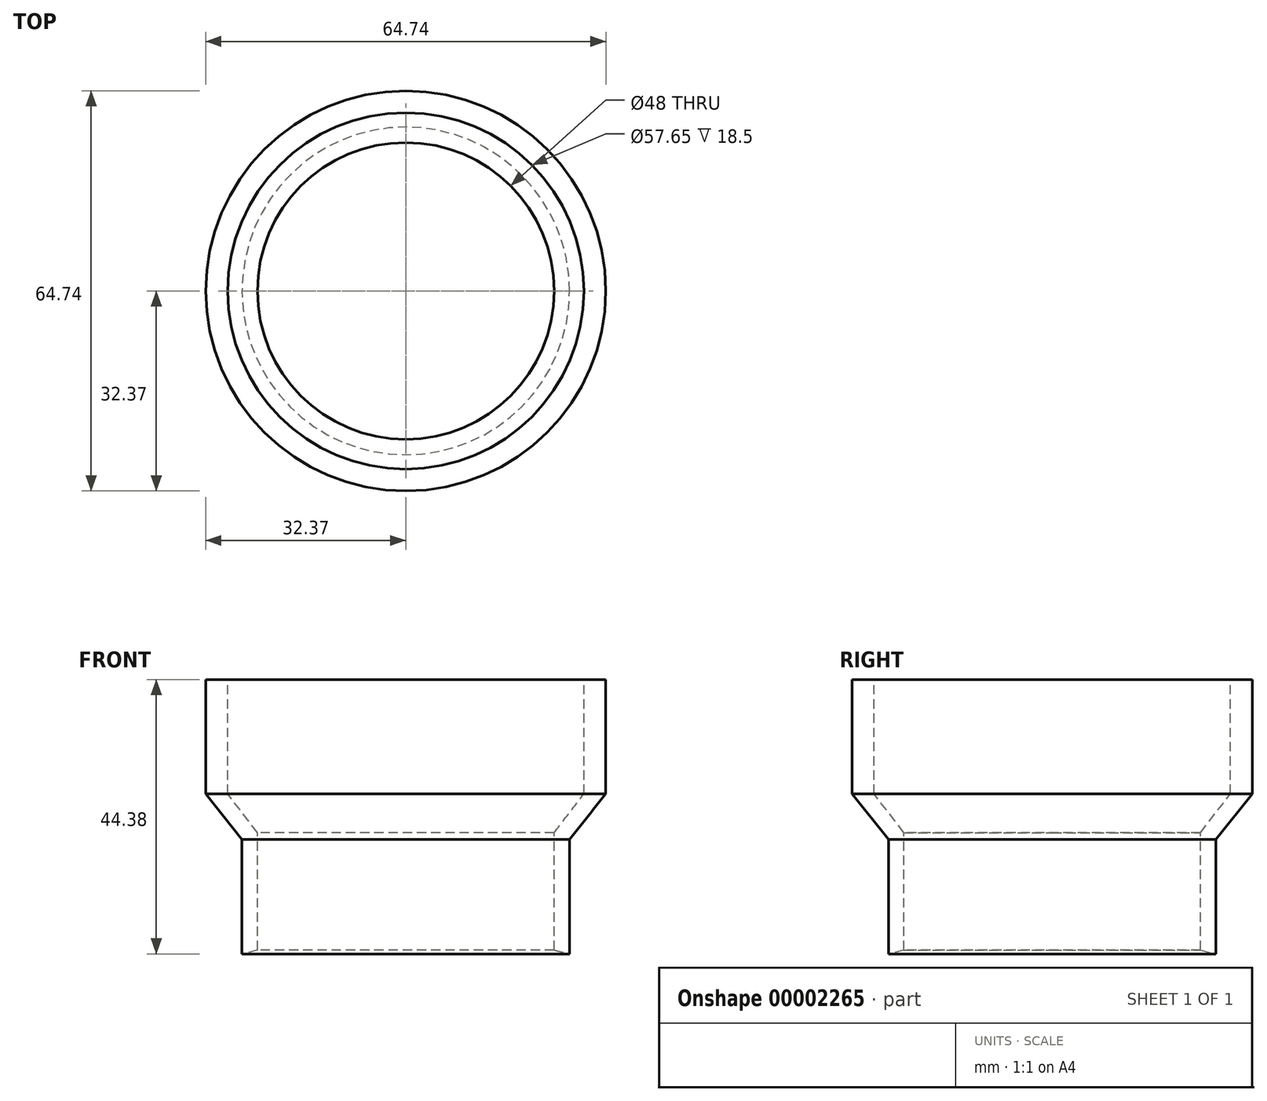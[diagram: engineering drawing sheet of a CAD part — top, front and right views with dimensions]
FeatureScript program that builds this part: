
annotation { "Feature Type Name" : "Feature", "Feature Type Description" : "" }
export const myFeature = defineFeature(function(context is Context, id is Id, definition is map)
    precondition{}
    {
        {
            var Q0;
            Q0=qCreatedBy(makeId("Front.planeOp"),FACE);
            var sketch = newSketch(context, id + "F0", { "sketchPlane" : qUnion([Q0])});
            skLineSegment(sketch, "E0", {"start": v(0, 38.12) * mm, "end": v(0, -26.84) * mm, "construction": true});
            skLineSegment(sketch, "E1", {"start": v(24, -25.27) * mm, "end": v(24, -6.27) * mm});
            skLineSegment(sketch, "E2", {"start": v(24, -6.27) * mm, "end": v(28.83, 0) * mm});
            skLineSegment(sketch, "E3", {"start": v(28.83, 0) * mm, "end": v(28.82, 18.5) * mm});
            skLineSegment(sketch, "E4", {"start": v(28.83, 18.5) * mm, "end": v(32.37, 18.5) * mm});
            skLineSegment(sketch, "E5", {"start": v(32.37, 18.5) * mm, "end": v(32.37, 0) * mm});
            skLineSegment(sketch, "E6", {"start": v(32.37, 0) * mm, "end": v(26.5, -7.38) * mm});
            skLineSegment(sketch, "E7", {"start": v(26.5, -7.38) * mm, "end": v(26.5, -25.88) * mm});
            skLineSegment(sketch, "E8", {"start": v(26.5, -25.88) * mm, "end": v(24, -25.27) * mm});
            skSolve(sketch);
        }
        {
            var Q0;
            Q0=makeQuery(id+"F0.imprint","IMPRINT",FACE,{"disambiguationData":[TD([[makeQuery(id+"F0.imprint","IMPRINT",EDGE,{"derivedFrom":sQuery(id+"F0.wireOp",EDGE,"E1")}),-1.0]])]});
            var Q1;
            Q1=sQuery(id+"F0.wireOp",EDGE,"E0");
            revolve(context, id + "F1", {"entities" : qUnion([Q0]), "axis" : qUnion([Q1]), "revolveType" : RevolveType.FULL});
        }
    });
